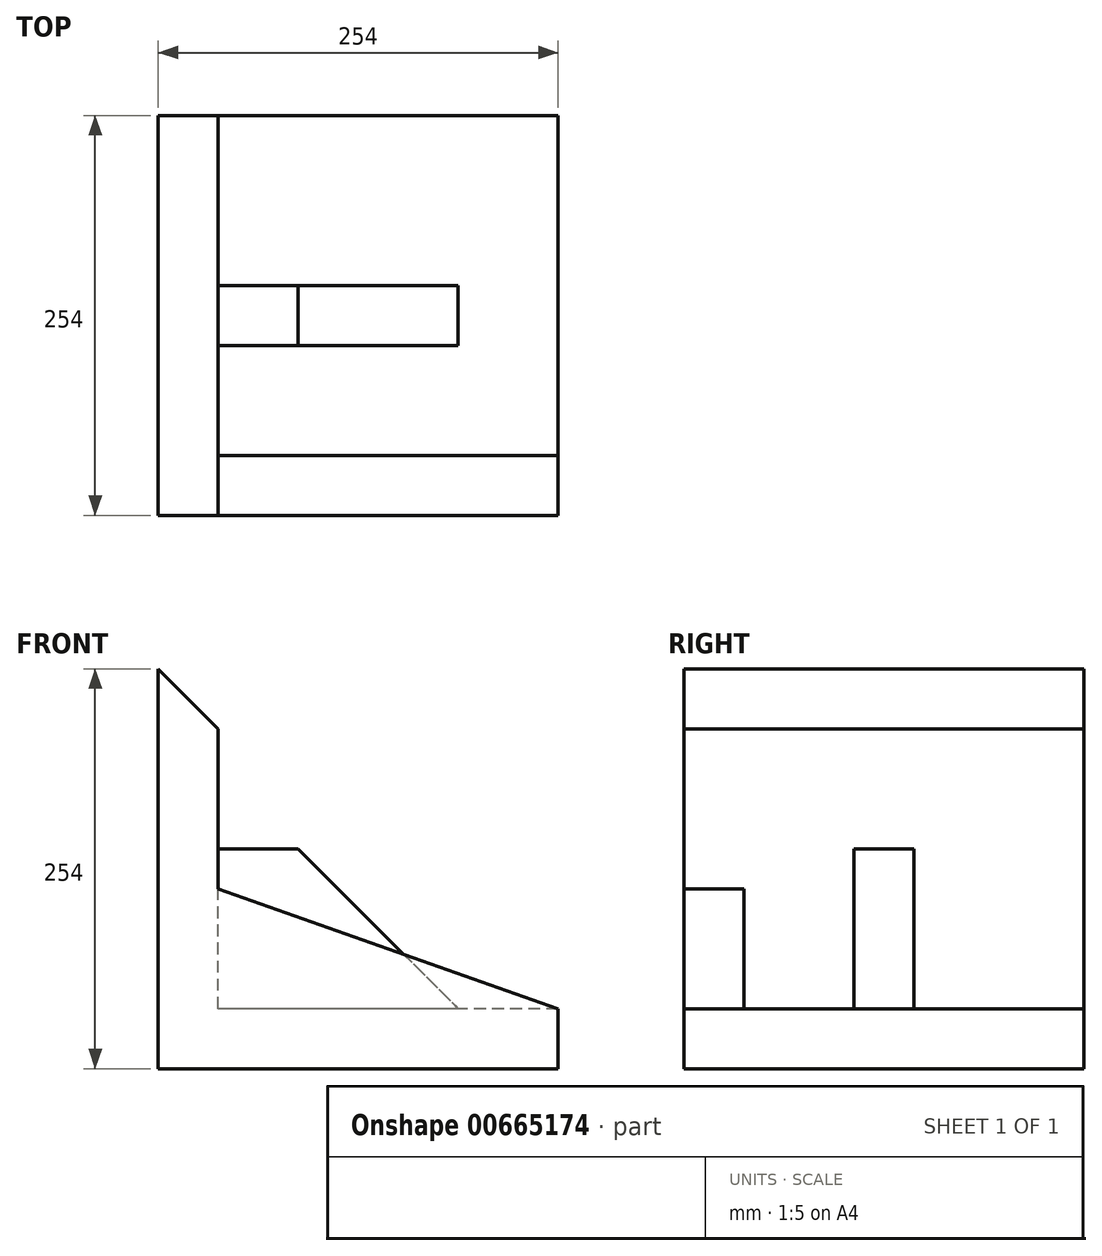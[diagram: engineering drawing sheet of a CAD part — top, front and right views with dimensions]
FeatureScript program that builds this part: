
annotation { "Feature Type Name" : "Feature", "Feature Type Description" : "" }
export const myFeature = defineFeature(function(context is Context, id is Id, definition is map)
    precondition{}
    {
        {
            var Q0;
            Q0=qCreatedBy(makeId("Front.planeOp"),FACE);
            var sketch = newSketch(context, id + "F0", { "sketchPlane" : qUnion([Q0])});
            skLineSegment(sketch, "E0", {"start": v(0, 0) * mm, "end": v(254, 0) * mm});
            skLineSegment(sketch, "E1", {"start": v(254, 0) * mm, "end": v(254, 38.1) * mm});
            skLineSegment(sketch, "E2", {"start": v(254, 38.1) * mm, "end": v(38.1, 38.1) * mm});
            skLineSegment(sketch, "E3", {"start": v(38.1, 38.1) * mm, "end": v(38.1, 215.9) * mm});
            skLineSegment(sketch, "E4", {"start": v(38.1, 215.9) * mm, "end": v(0, 254) * mm});
            skLineSegment(sketch, "E5", {"start": v(0, 254) * mm, "end": v(0, 0) * mm});
            skLineSegment(sketch, "E6", {"start": v(38.1, 139.7) * mm, "end": v(88.9, 139.7) * mm});
            skLineSegment(sketch, "E7", {"start": v(88.9, 139.7) * mm, "end": v(190.5, 38.1) * mm});
            skSolve(sketch);
        }
        {
            var Q0;
            Q0=makeQuery(id+"F0.imprint","IMPRINT",FACE,{"disambiguationData":[TD([[makeQuery(id+"F0.imprint","IMPRINT",EDGE,{"derivedFrom":sQuery(id+"F0.wireOp",EDGE,"E0")}),1.0]])]});
            extrude(context, id + "F1", {"entities" : qUnion([Q0]), "endBound" : BoundingType.SYMMETRIC, "depth" : 254 * mm, "offsetDistance" : 25.4 * mm});
        }
        {
            var Q0;
            Q0=makeQuery(id+"F1.opExtrude","CAP_FACE",FACE,{"disambiguationData":[OSD([sQuery(id+"F0.wireOp",EDGE,"E0"),sQuery(id+"F0.wireOp",EDGE,"E1"),sQuery(id+"F0.wireOp",EDGE,"E2"),sQuery(id+"F0.wireOp",EDGE,"E3"),sQuery(id+"F0.wireOp",EDGE,"E4"),sQuery(id+"F0.wireOp",EDGE,"E5")])],"isStart":false});
            var sketch = newSketch(context, id + "F2", { "sketchPlane" : qUnion([Q0])});
            skLineSegment(sketch, "E8", {"start": v(38.1, 114.3) * mm, "end": v(254, 38.1) * mm});
            skSolve(sketch);
        }
        {
            var Q0;
            {var subQ0=sQuery(id+"F2.wireOp",EDGE,"E8");Q0=makeQuery(id+"F2.imprint","IMPRINT",FACE,{"disambiguationData":[TD([[makeQuery(id+"F2.imprint","IMPRINT",EDGE,{"derivedFrom":subQ0}),-1.0]])]});}
            extrude(context, id + "F3", {"entities" : qUnion([Q0]), "operationType" : NewBodyOperationType.ADD, "oppositeDirection" : true, "depth" : 38.1 * mm, "offsetDistance" : 25.4 * mm});
        }
        {
            var Q0;
            {var subQ4=sQuery(id+"F0.wireOp",EDGE,"E6");Q0=makeQuery(id+"F0.imprint","IMPRINT",FACE,{"disambiguationData":[TD([[makeQuery(id+"F0.imprint","IMPRINT",EDGE,{"derivedFrom":subQ4}),-1.0]])]});}
            extrude(context, id + "F4", {"entities" : qUnion([Q0]), "operationType" : NewBodyOperationType.ADD, "endBound" : BoundingType.SYMMETRIC, "depth" : 38.1 * mm, "offsetDistance" : 25.4 * mm});
        }
    });
